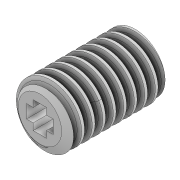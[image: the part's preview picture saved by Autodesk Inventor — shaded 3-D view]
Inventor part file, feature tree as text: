
AUTODESK INVENTOR PART (.ipt)
format: ipt  version: 2022 (Build 260153000, 153)  size: 997,376 bytes
history: native  units: in
note: dims shown in document units (in); Inventor stores cm internally (conversion verified against a paired STEP export)
features: extrude x2, sketch x2, projected_geometry x2, other x1
ambient origin geometry x8: Origin, YZ Plane, XZ Plane, XY Plane, X Axis, Y Axis, Z Axis, Center Point
bodies: Solid1 (feature_tree)
feature tree (7):
  extrude  "Extrusion1"  Depth=0.315in
  extrude  "Extrusion2"  Depth=0.0787in
  sketch  "Sketch1"  dims[d0=3.937in d1=0.0in d4=0.315in]
  projected_geometry  "Projected Loop1"
  projected_geometry  "Projected Loop2"
  sketch  "Sketch2"  dims[d5=0.315in d6=0.0787in d7=0.0787in d8=0.0787in d9=3.937in d10=0.0in]
  other  "Boss-Extrude1"
